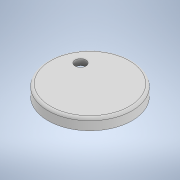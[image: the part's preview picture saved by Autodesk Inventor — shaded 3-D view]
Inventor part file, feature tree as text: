
AUTODESK INVENTOR PART (.ipt)
format: ipt  version: 2022 (Build 260153000, 153)  size: 157,184 bytes
history: native  units: in
note: dims shown in document units (in); Inventor stores cm internally (conversion verified against a paired STEP export)
features: sketch x3, extrude x2, revolve x1, fillet x1
ambient origin geometry x8: Origin, YZ Plane, XZ Plane, XY Plane, X Axis, Y Axis, Z Axis, Center Point
bodies: Solid1 (feature_tree)
feature tree (7):
  revolve  "Revolution1"  [1 undecoded]
  fillet  "Fillet1"  Radius=0.2402in
  extrude  "Extrusion1"  Depth=0.1575in
  extrude  "Extrusion2"  TaperAngle=90.0deg  [1 undecoded]
  sketch  "Sketch2"  dims[d0=1.9114in d1=0.1575in d2=0.2402in]
  sketch  "Sketch3"  dims[d3=0.5118in d4=0.1575in]
  sketch  "Sketch5"  dims[d5=0.2756in d6=90.0deg d7=0.1181in d8=1.3386in d9=1.1811in d11=360.0deg d13=0.2165in d14=0.0in d15=0.7815in d16=0.4921in d17=1.1811in d18=0.0in d19=0.0in d20=30.0deg]
note: 2 required parameter values undecoded (feature->parameter linkage not recoverable at this tier; creation-order binding heuristic only, values carry confidence <= 0.55)